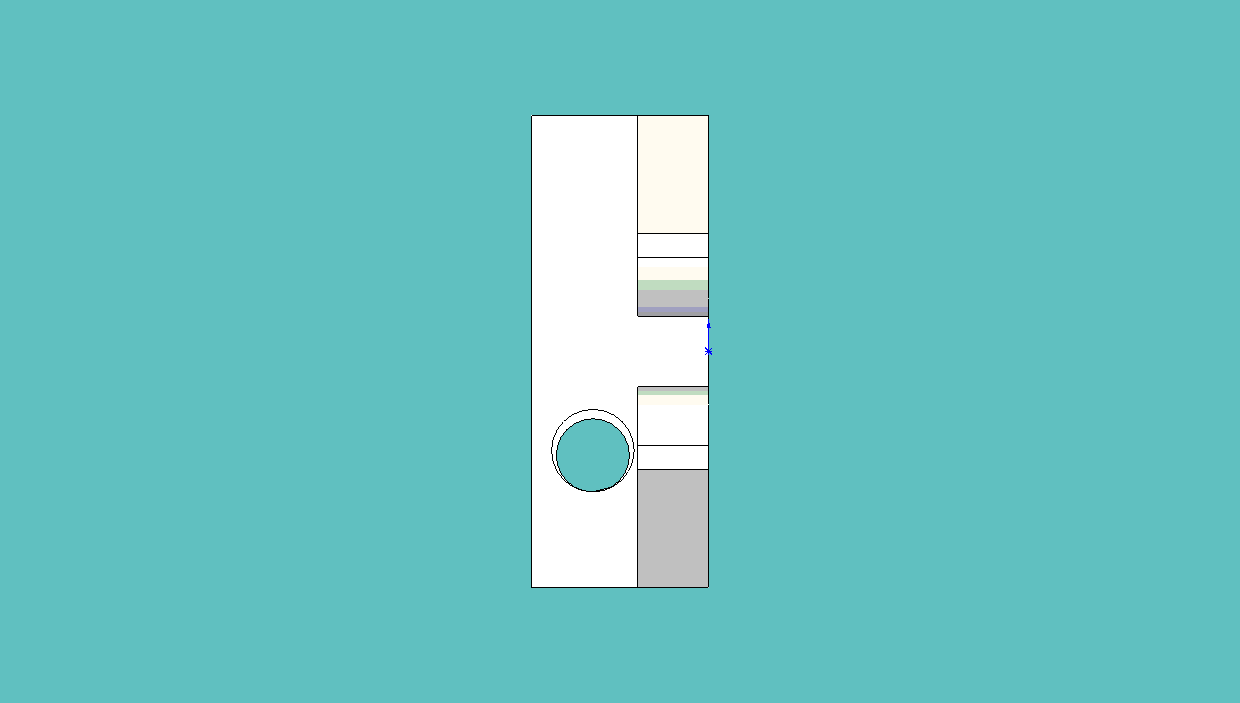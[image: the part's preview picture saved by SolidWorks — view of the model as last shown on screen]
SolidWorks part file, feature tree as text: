
SOLIDWORKS PART (.sldprt)
format: sldprt  version: not decoded by parser v0  size: 202,240 bytes
history: native  units: mm
features: sketch x6, plane x3, extrude x2, cut_extrude x2, material x1, fillet x1, chamfer x1, hole x1, thread x1 (+8 scaffold rows collapsed)
feature tree (26):
  scaffold x8  (default folders/planes/origin — collapsed)
  material  "Matériau <non spécifié>"
  plane  "Plan de face"
  plane  "Plan de dessus"
  plane  "Plan de droite"
  sketch  "Esquisse1"  dims[c1.D3=3.2mm c1.D4=5.2mm c1.D6=3.1mm c1.D7=3.1mm c1.D8=3.1mm c2.D4=3.2mm c2.D1=62.0mm c2.D2=40.0mm c3.D4=40.0mm c3.D5=20.0mm c3.D7=7.0mm c3.D8=3.5mm c4.D4=50.0mm]
  extrude  "Extrusion1"  Depth=15mm
  sketch  "Esquisse2"  dims[D1=10.0mm D2=10.0mm D3=6.0mm]
  extrude  "Extrusion2"  Depth=6mm
  fillet  "Congé1"  Radius=5mm
  chamfer  "Chanfrein1"  Distance=1.5mm Angle=45deg
  sketch  "Esquisse3"  dims[c1.D1=~5.146236mm c1.D2=~5.146236mm c1.D3=6.2mm c2.D1=9.8mm c2.D2=11.2mm]
  cut_extrude  "Enlèv. mat.-Extru.1"  [1 undecoded]
  sketch  "Esquisse4"  dims[D1=7.0mm]
  cut_extrude  "Enlèv. mat.-Extru.2"  Depth=10mm
  hole  "Trou taraudé M5x0.81"  Diameter=4.2mm Depth=22mm
  sketch  "Esquisse3D1"  dims[D1=7.5mm D2=26.2mm]
  sketch  "Esquisse5"  dims[hole-wizard template sketch: 47 standard entries collapsed; hole parameters kept: c15.Profondeur du trou pour taraudage=22.0mm c15.D3=~14.816244mm c15.Angle de pointe=118.0deg]
  thread  "Filetage de perçage1"  Diameter=20mm  [1 undecoded]
decode coverage: 13 of 14 modeling features carry decoded parameters
note: ~ marks probable driven/reference dimensions
note: 2 parameter values undecoded
note: suppression state not decoded; provenance and decode notes live in map.json
